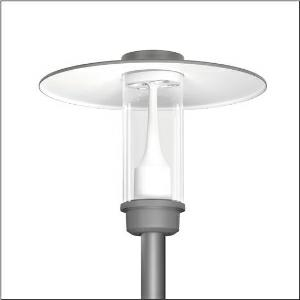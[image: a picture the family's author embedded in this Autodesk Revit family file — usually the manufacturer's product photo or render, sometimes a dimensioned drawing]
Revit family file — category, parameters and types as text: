
# Revit family: litepole_2_iq___p1_0a_5xa5425bf14hp_e9a6
name_source: partatom
category: Lighting Fixtures
units: mm (PartAtom-declared; Revit-internal decimal feet)

## family parameters
Cut with Voids When Loaded = No
Host = Face
Light Source = No
Part Type = Normal
Room Calculation Point = No
Round Connector Dimension = Use Diameter
Shared = No

## types (1)
- --- (1 x LED, 3910 lm, 33.6 W, 2200K)
    Apparent Load = 34 VA
    CIE Flux Codes = 32 62 90 96 100
    Color Rendering = 70
    Color Temperature = 2200K
    Default Elevation = 1800 mm
    Description = Litepole 2 iQ, mast luminaire, Module 540 iQ-SR, primary light control with 3 zone facetted reflector, of plastic, silver coated, highly specular, structured, primary optical cover: cover, of PMMA, transparent, light distribution: P1.0a, light emission: direct distribution, primary light characteristic: strongly asymmetric, installation type: post-top, LED, High Power LED, rated luminous flux: 3.910lm, luminous efficacy: 116lm/W, light colour: 722, colour temperature: 2200K, control gear: iQ Street-Remote, control: pre-setting: logarithmic dimming characteristic, Street-Remote, Auto-Match, Temp-Guard, Lumen-Switch, Night-Set, Smart-Wire, Light-Fading, Desk-Remote (wireless, voltage-free reading and setting of iQ features in the workshop via application-optimized NFC function/RFID function), optimised constant luminous flux control (CLO 2.0), with terminal, 6-pole, max. 2.5mm², mains connection: 230..240V, AC, 50/60Hz, start of lifetime: 34W, end of service life: 36W, reduction: 15W, luminaire housing, upper part, of aluminium, coated, Siteco® metallic grey (DB 702S), diameter: 750mm, height: 590mm, spigot size: d x l = 76 x 70mm (post-top) | with reducer (optional accessory) 60 x 70mm, mounting height: 3..5m, post-top mast mounting element, of diecast aluminium, coated, Siteco® metallic grey (DB 702S), Module 540 iQ-SR, traffic white (RAL 9016), equipment: Power, protection rating (complete): IP65, insulation class (complete): insulation class II (safety insulation), certification: CE, ENEC, VDE, packaging unit: 1 piece

Light Distribution: P1.0a
    Height = 590 mm
    Lamp = 1 x LED
    Lamp Light Flux = 3910 lm
    Lamp Power = 33.6 W
    Lamp count = 1
    Length = 750 mm
    Luminous efficacy = 116 lm/W
    Manufacturer = Siteco
    ModVariant = No
    Model = 5XA5425BF14HP
    Number of Poles = 1
    OnlyDefault = Yes
    Power Factor = 1
    Product Name = Litepole 2 iQ | P1.0a
    Product group = mast luminaire | pylon top
    ProductGroupID = 6100
    Protection Class = Protection class II
    Protection Degree = IP 65
    RLX_Detail_Level = 1
    RLX_Emergency_Light_Flux = 0 lm
    RLX_Emergency_Type = 0
    RLX_Emergency_Type_DB = No
    RlxData = <blob elided: 32065 chars, md5=c07d514c>
    Socket = socket
    Standby Power = 0 W
    System Light Flux = 3910 lm
    System Power = 34 W
    Type Comments = factory setting: luminous flux: 100 % | dim-lin: 254 | 695 mA
    Type Image = l_1006518.jpg
    URL = http://relux.com
    VarID = @adj_192410
    Voltage = 0 V
    Weight = 0.00 kg
    Width = 0 mm  [stored 0 ft]

note: [stored X ft] marks values corroborated as IEEE doubles in the binary element streams (Revit-internal decimal feet)

## geometry (parser evidence)
native form markers: Blend x4, Sweep x11
no freeform markers — native parametric forms only
